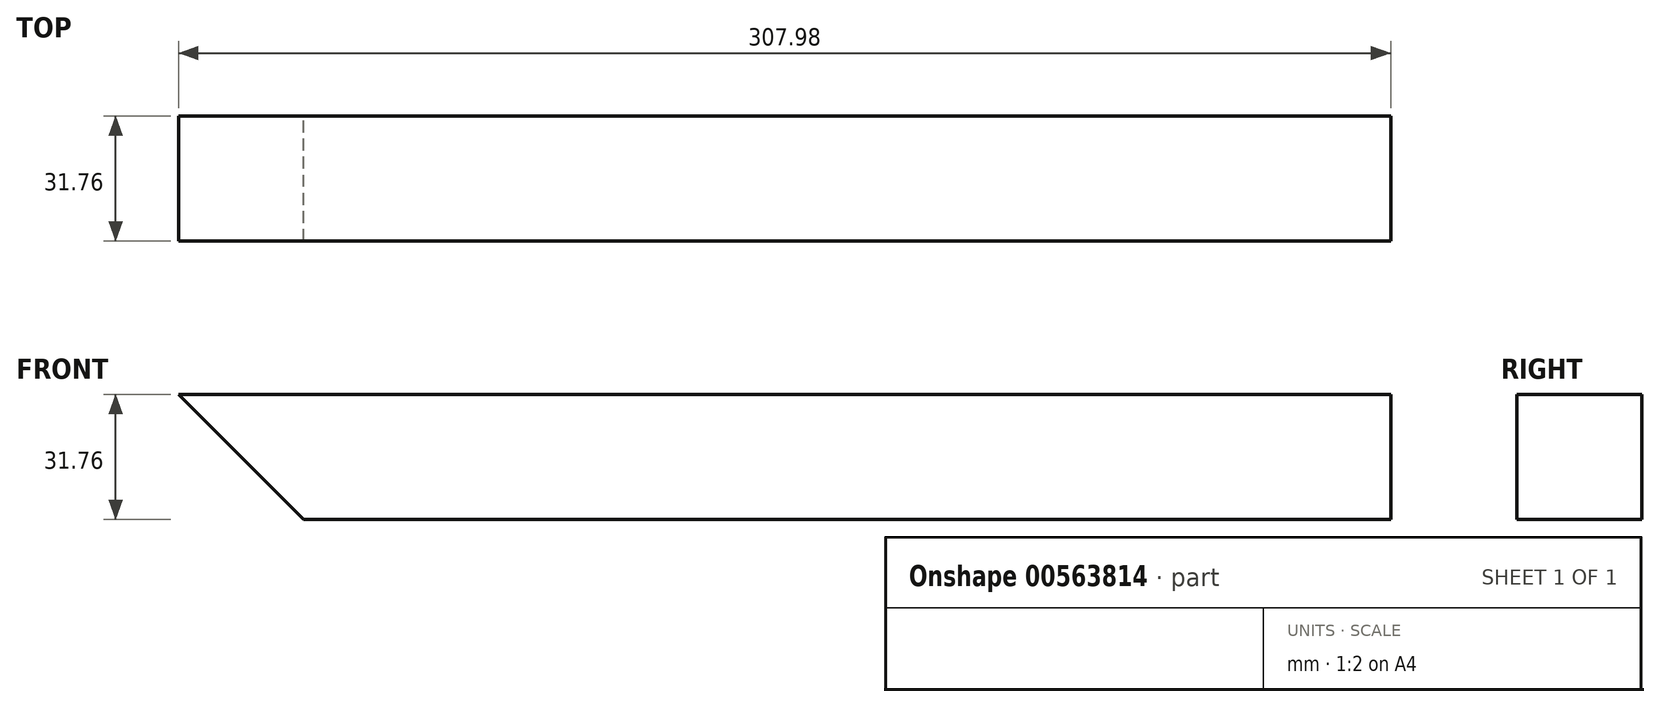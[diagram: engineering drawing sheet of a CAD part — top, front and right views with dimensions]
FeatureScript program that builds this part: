
annotation { "Feature Type Name" : "Feature", "Feature Type Description" : "" }
export const myFeature = defineFeature(function(context is Context, id is Id, definition is map)
    precondition{}
    {
        {
            var Q0;
            Q0=qCreatedBy(makeId("Front.planeOp"),FACE);
            var sketch = newSketch(context, id + "F0", { "sketchPlane" : qUnion([Q0])});
            skLineSegment(sketch, "E0.bottom", {"start": v(-153.99, 15.88) * mm, "end": v(153.99, 15.88) * mm});
            skLineSegment(sketch, "E0.top", {"start": v(-153.99, -15.87) * mm, "end": v(153.99, -15.87) * mm});
            skLineSegment(sketch, "E0.left", {"start": v(-153.99, 15.88) * mm, "end": v(-153.99, -15.87) * mm});
            skLineSegment(sketch, "E0.right", {"start": v(153.99, 15.88) * mm, "end": v(153.99, -15.87) * mm});
            skPoint(sketch, "E0.middle", {"position": v(0, 0) * mm});
            skLineSegment(sketch, "E1", {"start": v(-153.99, 15.88) * mm, "end": v(-122.24, -15.87) * mm});
            skSolve(sketch);
        }
        {
            var Q0;
            Q0=makeQuery(id+"F0.imprint","IMPRINT",FACE,{"disambiguationData":[TD([[makeQuery(id+"F0.imprint","IMPRINT",EDGE,{"derivedFrom":sQuery(id+"F0.wireOp",EDGE,"E0.bottom")}),-1.0]])]});
            extrude(context, id + "F1", {"entities" : qUnion([Q0]), "endBound" : BoundingType.SYMMETRIC, "depth" : 31.75 * mm, "offsetDistance" : 25.4 * mm});
        }
    });
